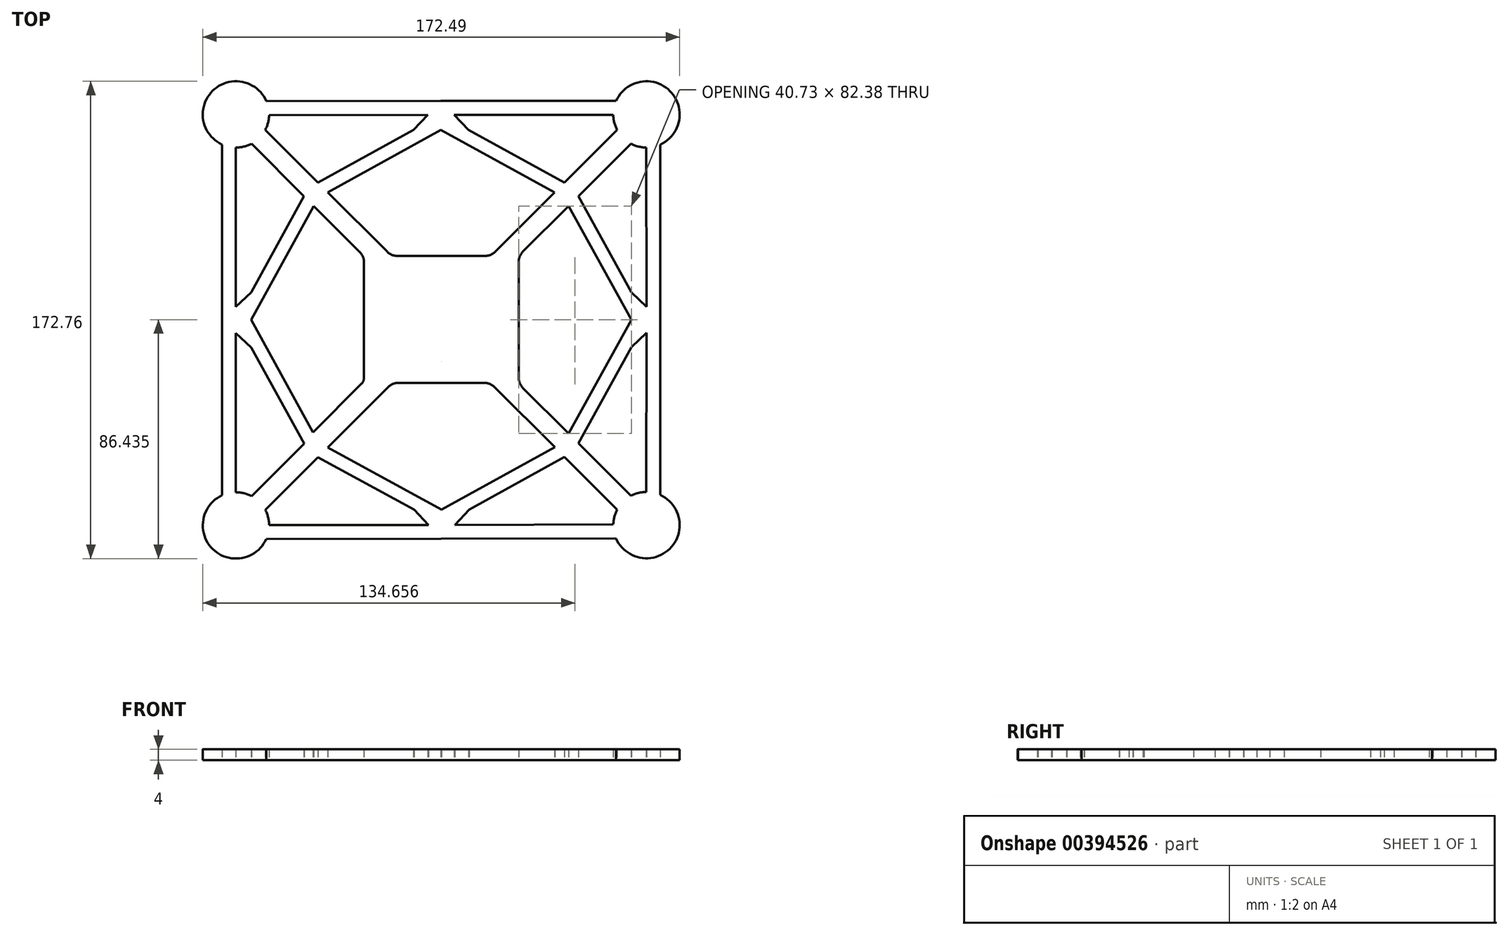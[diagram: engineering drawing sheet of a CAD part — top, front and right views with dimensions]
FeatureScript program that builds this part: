
annotation { "Feature Type Name" : "Feature", "Feature Type Description" : "" }
export const myFeature = defineFeature(function(context is Context, id is Id, definition is map)
    precondition{}
    {
        {
            var Q0;
            Q0=qCreatedBy(makeId("Top.planeOp"),FACE);
            var sketch = newSketch(context, id + "F0", { "sketchPlane" : qUnion([Q0])});
            skPoint(sketch, "E0", {"position": v(0, 0) * mm});
            skArc(sketch, "E1", {"start": v(88.6, 83.6) * mm, "mid": v(91.24, 82.57) * mm, "end": v(94.06, 82.2) * mm});
            skLineSegment(sketch, "E2", {"start": v(20, 20) * mm, "end": v(20, 19.87) * mm});
            skLineSegment(sketch, "E3", {"start": v(20, 19.87) * mm, "end": v(20, 20) * mm});
            skLineSegment(sketch, "E4", {"start": v(19.95, 19.87) * mm, "end": v(20.05, 19.87) * mm});
            skPoint(sketch, "E5.orphan", {"position": v(40, 0) * mm});
            skPoint(sketch, "E6.orphan", {"position": v(20, 0) * mm});
            skPoint(sketch, "E7.orphan", {"position": v(0, 40) * mm});
            skLineSegment(sketch, "E8", {"start": v(83.6, 88.6) * mm, "end": v(64.56, 69.56) * mm});
            skLineSegment(sketch, "E9", {"start": v(88.6, 83.6) * mm, "end": v(69.6, 64.6) * mm});
            skPoint(sketch, "E9.endSnap0", {"position": v(40, 29.94) * mm});
            skLineSegment(sketch, "E10", {"start": v(99.2, 83.3) * mm, "end": v(99.2, 19.85) * mm});
            skLineSegment(sketch, "E11", {"start": v(69.6, 64.6) * mm, "end": v(88.74, 29.81) * mm});
            skPoint(sketch, "E12", {"position": v(66.07, 61.07) * mm});
            skLineSegment(sketch, "E13", {"start": v(66.07, 61.07) * mm, "end": v(88.74, 19.85) * mm});
            skPoint(sketch, "E14.orphan", {"position": v(40, 40) * mm});
            skLineSegment(sketch, "E15.trimOffspring", {"start": v(66.07, 61.07) * mm, "end": v(49.46, 44.46) * mm});
            skPoint(sketch, "E16.orphan", {"position": v(99.2, 94.2) * mm});
            skLineSegment(sketch, "E17.trimOffspring", {"start": v(94.06, 82.2) * mm, "end": v(94.21, 24.6) * mm});
            skLineSegment(sketch, "E18.MirrorCS", {"start": v(66.07, -21.32) * mm, "end": v(49.46, -4.71) * mm});
            skLineSegment(sketch, "E19.MirrorCS", {"start": v(83.6, -48.84) * mm, "end": v(64.57, -29.82) * mm});
            skLineSegment(sketch, "E20.MirrorCS", {"start": v(88.6, -43.84) * mm, "end": v(69.6, -24.85) * mm});
            skLineSegment(sketch, "E21.MirrorCS", {"start": v(66.07, -21.32) * mm, "end": v(88.74, 19.9) * mm});
            skLineSegment(sketch, "E22.MirrorCS", {"start": v(69.6, -24.85) * mm, "end": v(88.74, 9.93) * mm});
            skLineSegment(sketch, "E23.MirrorCS", {"start": v(94.06, -42.45) * mm, "end": v(94.21, 15.12) * mm});
            skLineSegment(sketch, "E24.MirrorCS", {"start": v(99.2, -43.54) * mm, "end": v(99.2, 19.9) * mm});
            skArc(sketch, "E25.MirrorCS", {"start": v(99.2, -43.54) * mm, "mid": v(102.6, -63.03) * mm, "end": v(83.2, -59.22) * mm});
            skLineSegment(sketch, "E26.MirrorCS", {"start": v(-43.68, -48.93) * mm, "end": v(-24.6, -29.86) * mm});
            skLineSegment(sketch, "E27.MirrorCS", {"start": v(-48.67, -43.95) * mm, "end": v(-29.65, -24.94) * mm});
            skLineSegment(sketch, "E28.MirrorCS", {"start": v(-26.43, -20.85) * mm, "end": v(-8.88, -3.3) * mm});
            skLineSegment(sketch, "E29.MirrorCS", {"start": v(-29.65, -24.94) * mm, "end": v(-48.8, 9.87) * mm});
            skArc(sketch, "E30.MirrorCS", {"start": v(-59.29, -43.66) * mm, "mid": v(-62.72, -63.08) * mm, "end": v(-43.33, -59.48) * mm});
            skLineSegment(sketch, "E31.MirrorCS", {"start": v(-54.29, -42.54) * mm, "end": v(-54.29, 15.08) * mm});
            skLineSegment(sketch, "E32.MirrorCS", {"start": v(-54.29, -42.56) * mm, "end": v(-54.29, 15.08) * mm});
            skLineSegment(sketch, "E33.MirrorCS", {"start": v(-59.29, -43.66) * mm, "end": v(-59.29, 19.83) * mm});
            skLineSegment(sketch, "E34.MirrorCS", {"start": v(-26.13, 61.04) * mm, "end": v(-48.8, 19.83) * mm});
            skLineSegment(sketch, "E35.MirrorCS", {"start": v(-29.67, 64.58) * mm, "end": v(-48.8, 29.8) * mm});
            skLineSegment(sketch, "E36.MirrorCS", {"start": v(-54.29, 82.2) * mm, "end": v(-54.29, 24.58) * mm});
            skLineSegment(sketch, "E37.MirrorCS", {"start": v(-59.29, 83.3) * mm, "end": v(-59.29, 19.83) * mm});
            skArc(sketch, "E38.MirrorCS", {"start": v(-59.29, 83.3) * mm, "mid": v(-62.69, 102.78) * mm, "end": v(-43.28, 98.97) * mm});
            skLineSegment(sketch, "E39.MirrorCS", {"start": v(-43.68, 88.6) * mm, "end": v(-24.61, 69.52) * mm});
            skLineSegment(sketch, "E40.MirrorCS", {"start": v(20.05, 19.87) * mm, "end": v(19.95, 19.87) * mm});
            skLineSegment(sketch, "E41.MirrorCS", {"start": v(-21.14, -26.28) * mm, "end": v(20.12, -48.9) * mm});
            skLineSegment(sketch, "E42.MirrorCS", {"start": v(-24.6, -29.86) * mm, "end": v(10.12, -48.9) * mm});
            skLineSegment(sketch, "E43.MirrorCS", {"start": v(-42.27, -54.48) * mm, "end": v(15.37, -54.38) * mm});
            skLineSegment(sketch, "E44.MirrorCS", {"start": v(64.62, 69.53) * mm, "end": v(29.83, 88.6) * mm});
            skLineSegment(sketch, "E45.MirrorCS", {"start": v(61.1, 65.99) * mm, "end": v(19.84, 88.6) * mm});
            skLineSegment(sketch, "E46.MirrorCS", {"start": v(82.2, 94.1) * mm, "end": v(24.6, 94.09) * mm});
            skLineSegment(sketch, "E47.MirrorCS", {"start": v(-24.61, 69.52) * mm, "end": v(9.91, 88.6) * mm});
            skLineSegment(sketch, "E48.MirrorCS", {"start": v(-21.08, 66) * mm, "end": v(19.84, 88.6) * mm});
            skLineSegment(sketch, "E49.MirrorCS", {"start": v(-42.3, 93.97) * mm, "end": v(15.09, 94.07) * mm});
            skLineSegment(sketch, "E50.MirrorCS", {"start": v(-43.28, 98.97) * mm, "end": v(19.82, 99.08) * mm});
            skLineSegment(sketch, "E51.MirrorCS", {"start": v(61.03, -26.28) * mm, "end": v(20.12, -48.9) * mm});
            skLineSegment(sketch, "E52.MirrorCS", {"start": v(64.57, -29.82) * mm, "end": v(30.05, -48.9) * mm});
            skPoint(sketch, "E53.orphan", {"position": v(20, 19.87) * mm});
            skPoint(sketch, "E54.orphan", {"position": v(20, 40) * mm});
            skPoint(sketch, "E55.orphan", {"position": v(0, 19.87) * mm});
            skLineSegment(sketch, "E56.trimOffspring", {"start": v(-21.07, -26.32) * mm, "end": v(0.79, -4.46) * mm});
            skArc(sketch, "E57.trimOffspring", {"start": v(-42.3, 93.97) * mm, "mid": v(-42.67, 91.2) * mm, "end": v(-43.68, 88.6) * mm});
            skPoint(sketch, "E58.MirrorCS.start.orphan", {"position": v(-26.09, 61.09) * mm});
            skPoint(sketch, "E59.MirrorCS.end.orphan", {"position": v(-29.62, 64.62) * mm});
            skPoint(sketch, "E59.MirrorCS.start.orphan", {"position": v(-48.68, 83.6) * mm});
            skLineSegment(sketch, "E60.trimOffspring", {"start": v(-21.08, 66) * mm, "end": v(1.91, 43) * mm});
            skLineSegment(sketch, "E61.trimOffspring", {"start": v(61.02, 66.02) * mm, "end": v(39.46, 44.46) * mm});
            skArc(sketch, "E62", {"start": v(94.06, -42.45) * mm, "mid": v(91.24, -42.82) * mm, "end": v(88.6, -43.84) * mm});
            skArc(sketch, "E63.trimOffspring", {"start": v(83.6, -48.84) * mm, "mid": v(82.58, -51.45) * mm, "end": v(82.2, -54.22) * mm});
            skArc(sketch, "E64.trimOffspring", {"start": v(82.2, 94.1) * mm, "mid": v(82.57, 91.26) * mm, "end": v(83.6, 88.6) * mm});
            skArc(sketch, "E65", {"start": v(-43.28, 98.97) * mm, "mid": v(-62.69, 102.78) * mm, "end": v(-59.29, 83.3) * mm});
            skArc(sketch, "E66.trimOffspring", {"start": v(-43.68, 88.6) * mm, "mid": v(-42.67, 91.2) * mm, "end": v(-42.3, 93.97) * mm});
            skArc(sketch, "E67.trimOffspring", {"start": v(-54.29, 82.2) * mm, "mid": v(-51.4, 82.56) * mm, "end": v(-48.68, 83.6) * mm});
            skArc(sketch, "E68.trimOffspring", {"start": v(-48.67, -43.95) * mm, "mid": v(-51.4, -42.9) * mm, "end": v(-54.29, -42.56) * mm});
            skLineSegment(sketch, "E69", {"start": v(-48.8, 29.8) * mm, "end": v(-54.29, 24.58) * mm});
            skLineSegment(sketch, "E70", {"start": v(-48.8, 9.87) * mm, "end": v(-54.29, 15.08) * mm});
            skPoint(sketch, "E71.orphan", {"position": v(-54.29, 19.83) * mm});
            skLineSegment(sketch, "E72", {"start": v(24.6, 94.09) * mm, "end": v(29.83, 88.6) * mm});
            skLineSegment(sketch, "E73", {"start": v(15.09, 94.07) * mm, "end": v(9.91, 88.6) * mm});
            skLineSegment(sketch, "E74.trimOffspring", {"start": v(61.03, -26.28) * mm, "end": v(39.21, -4.46) * mm});
            skLineSegment(sketch, "E75", {"start": v(88.74, 29.81) * mm, "end": v(94.21, 24.6) * mm});
            skLineSegment(sketch, "E76", {"start": v(94.21, 15.12) * mm, "end": v(88.74, 9.93) * mm});
            skPoint(sketch, "E77.orphan", {"position": v(94.22, 19.9) * mm});
            skPoint(sketch, "E78.orphan", {"position": v(94.22, 19.85) * mm});
            skLineSegment(sketch, "E79", {"start": v(30.05, -48.9) * mm, "end": v(24.87, -54.36) * mm});
            skLineSegment(sketch, "E80", {"start": v(15.37, -54.38) * mm, "end": v(10.12, -48.9) * mm});
            skLineSegment(sketch, "E81", {"start": v(-9.46, 44.38) * mm, "end": v(-26.13, 61.04) * mm});
            skLineSegment(sketch, "E82.trimOffspring", {"start": v(-21.08, 66) * mm, "end": v(0.45, 44.46) * mm});
            skPoint(sketch, "E83.orphan", {"position": v(-29.67, 64.58) * mm});
            skLineSegment(sketch, "E84", {"start": v(-48.68, 83.6) * mm, "end": v(-29.67, 64.58) * mm});
            skPoint(sketch, "E85.MirrorCS.start.orphan", {"position": v(20, -0.25) * mm});
            skArc(sketch, "E86", {"start": v(20.03, 4.75) * mm, "mid": v(20.06, 4.75) * mm, "end": v(20.1, 4.75) * mm});
            skPoint(sketch, "E87.cCircle.perimeterSnap0", {"position": v(40, 12.31) * mm});
            skLineSegment(sketch, "E87.0", {"start": v(20.1, 4.75) * mm, "end": v(20.06, 4.73) * mm});
            skPoint(sketch, "E87.0.startSnap0", {"position": v(40, 12.31) * mm});
            skLineSegment(sketch, "E87.1", {"start": v(20.06, 4.73) * mm, "end": v(20.03, 4.75) * mm});
            skPoint(sketch, "E88.orphan", {"position": v(33.17, 12.31) * mm});
            skLineSegment(sketch, "E89.bottom", {"start": v(35.93, 43) * mm, "end": v(3.98, 43) * mm});
            skLineSegment(sketch, "E89.top", {"start": v(48, -3) * mm, "end": v(47.75, -3) * mm});
            skLineSegment(sketch, "E89.left", {"start": v(48, 40.93) * mm, "end": v(48, -1.18) * mm});
            skLineSegment(sketch, "E89.right", {"start": v(-8, 40.84) * mm, "end": v(-8, -1.18) * mm});
            skPoint(sketch, "E90.MirrorCS.end.orphan", {"position": v(35, -0.25) * mm});
            skPoint(sketch, "E91.orphan", {"position": v(40, 4.75) * mm});
            skPoint(sketch, "E92.MirrorCS.start.orphan", {"position": v(40, 19.87) * mm});
            skPoint(sketch, "E93.orphan", {"position": v(40, 35) * mm});
            skPoint(sketch, "E94.top.end.orphan", {"position": v(35, 40) * mm});
            skLineSegment(sketch, "E95.trimOffspring", {"start": v(-7.75, -3) * mm, "end": v(-8, -3) * mm});
            skLineSegment(sketch, "E96.trimOffspring", {"start": v(35.68, -3) * mm, "end": v(4.32, -3) * mm});
            skPoint(sketch, "E97.orphan", {"position": v(4.96, 39.96) * mm});
            skPoint(sketch, "E98.visualSharp", {"position": v(1.91, 43) * mm});
            skArc(sketch, "E98.filletArc", {"start": v(0.45, 44.46) * mm, "mid": v(2.07, 43.38) * mm, "end": v(3.98, 43) * mm});
            skPoint(sketch, "E99.newPointB", {"position": v(-8, 43) * mm});
            skArc(sketch, "E99.filletArc", {"start": v(-8, 40.84) * mm, "mid": v(-8.38, 42.76) * mm, "end": v(-9.46, 44.38) * mm});
            skPoint(sketch, "E100.visualSharp", {"position": v(38, 43) * mm});
            skArc(sketch, "E100.filletArc", {"start": v(35.93, 43) * mm, "mid": v(37.84, 43.38) * mm, "end": v(39.46, 44.46) * mm});
            skPoint(sketch, "E101.visualSharp", {"position": v(48, 43) * mm});
            skArc(sketch, "E101.filletArc", {"start": v(49.46, 44.46) * mm, "mid": v(48.38, 42.84) * mm, "end": v(48, 40.93) * mm});
            skArc(sketch, "E102.filletArc", {"start": v(48, -1.18) * mm, "mid": v(48.38, -3.1) * mm, "end": v(49.46, -4.71) * mm});
            skPoint(sketch, "E103.visualSharp", {"position": v(37.75, -3) * mm});
            skArc(sketch, "E103.filletArc", {"start": v(39.21, -4.46) * mm, "mid": v(37.6, -3.38) * mm, "end": v(35.68, -3) * mm});
            skPoint(sketch, "E104.visualSharp", {"position": v(2.25, -3) * mm});
            skArc(sketch, "E104.filletArc", {"start": v(4.32, -3) * mm, "mid": v(2.4, -3.38) * mm, "end": v(0.79, -4.46) * mm});
            skArc(sketch, "E105.filletArc", {"start": v(-8.88, -3.3) * mm, "mid": v(-8.23, -2.33) * mm, "end": v(-8, -1.18) * mm});
            skLineSegment(sketch, "E106", {"start": v(24.87, -54.36) * mm, "end": v(82.2, -54.22) * mm});
            skArc(sketch, "E107.converted", {"start": v(-42.27, -54.48) * mm, "mid": v(-42.64, -51.62) * mm, "end": v(-43.68, -48.93) * mm});
            skLineSegment(sketch, "E108", {"start": v(-43.33, -59.48) * mm, "end": v(83.2, -59.22) * mm});
            skLineSegment(sketch, "E109", {"start": v(-29.67, 64.58) * mm, "end": v(-24.61, 69.52) * mm});
            skLineSegment(sketch, "E110.trimOffspring", {"start": v(-26.43, -20.85) * mm, "end": v(-48.8, 19.83) * mm});
            skPoint(sketch, "E111.end.orphan", {"position": v(19.93, -59.35) * mm});
            skLineSegment(sketch, "E112", {"start": v(19.82, 99.08) * mm, "end": v(83.24, 99.08) * mm});
            skArc(sketch, "E113.trimOffspring", {"start": v(99.2, 83.3) * mm, "mid": v(102.64, 102.74) * mm, "end": v(83.24, 99.08) * mm});
            skSolve(sketch);
        }
        {
            var Q0;
            Q0 = qSketchRegion(id + "F0", true);
            extrude(context, id + "F1", {"entities" : qUnion([Q0]), "depth" : 4 * mm});
        }
    });
